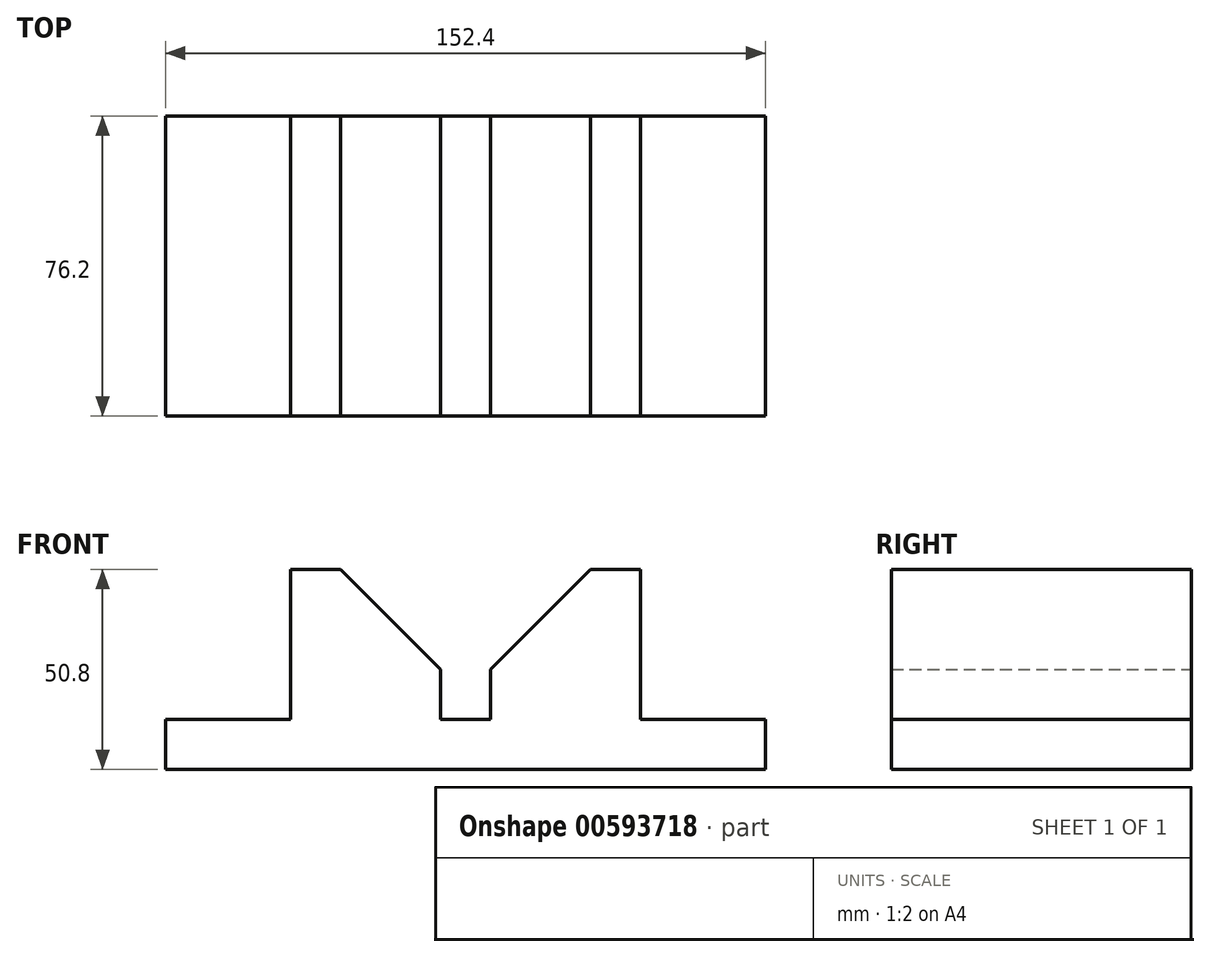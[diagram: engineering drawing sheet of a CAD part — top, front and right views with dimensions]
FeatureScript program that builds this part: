
annotation { "Feature Type Name" : "Feature", "Feature Type Description" : "" }
export const myFeature = defineFeature(function(context is Context, id is Id, definition is map)
    precondition{}
    {
        {
            var Q0;
            Q0=qCreatedBy(makeId("Front.planeOp"),FACE);
            var sketch = newSketch(context, id + "F0", { "sketchPlane" : qUnion([Q0])});
            skLineSegment(sketch, "E0", {"start": v(0, 0) * mm, "end": v(76.2, 0) * mm});
            skLineSegment(sketch, "E1", {"start": v(0, 0) * mm, "end": v(-76.2, 0) * mm});
            skLineSegment(sketch, "E2", {"start": v(-76.2, 0) * mm, "end": v(-76.2, 12.7) * mm});
            skLineSegment(sketch, "E3", {"start": v(-76.2, 12.7) * mm, "end": v(-44.45, 12.7) * mm});
            skLineSegment(sketch, "E4", {"start": v(-44.45, 12.7) * mm, "end": v(-44.45, 50.8) * mm});
            skLineSegment(sketch, "E5", {"start": v(-44.45, 50.8) * mm, "end": v(-31.75, 50.8) * mm});
            skLineSegment(sketch, "E6", {"start": v(76.2, 0) * mm, "end": v(76.2, 12.7) * mm});
            skLineSegment(sketch, "E7", {"start": v(76.2, 12.7) * mm, "end": v(44.45, 12.7) * mm});
            skLineSegment(sketch, "E8", {"start": v(44.45, 12.7) * mm, "end": v(44.45, 50.8) * mm});
            skLineSegment(sketch, "E9", {"start": v(44.45, 50.8) * mm, "end": v(31.75, 50.8) * mm});
            skLineSegment(sketch, "E10", {"start": v(0, 12.7) * mm, "end": v(-6.35, 12.7) * mm});
            skLineSegment(sketch, "E11", {"start": v(-6.35, 12.7) * mm, "end": v(-6.35, 25.4) * mm});
            skLineSegment(sketch, "E12", {"start": v(-6.35, 25.4) * mm, "end": v(-31.75, 50.8) * mm});
            skLineSegment(sketch, "E13", {"start": v(0, 12.7) * mm, "end": v(6.35, 12.7) * mm});
            skLineSegment(sketch, "E14", {"start": v(6.35, 12.7) * mm, "end": v(6.35, 25.4) * mm});
            skLineSegment(sketch, "E15", {"start": v(6.35, 25.4) * mm, "end": v(31.75, 50.8) * mm});
            skSolve(sketch);
        }
        {
            var Q0;
            Q0=makeQuery(id+"F0.imprint","IMPRINT",FACE,{"disambiguationData":[TD([[makeQuery(id+"F0.imprint","IMPRINT",EDGE,{"derivedFrom":sQuery(id+"F0.wireOp",EDGE,"E0")}),1.0]])]});
            extrude(context, id + "F1", {"entities" : qUnion([Q0]), "depth" : 76.2 * mm, "offsetDistance" : 25.4 * mm});
        }
    });
